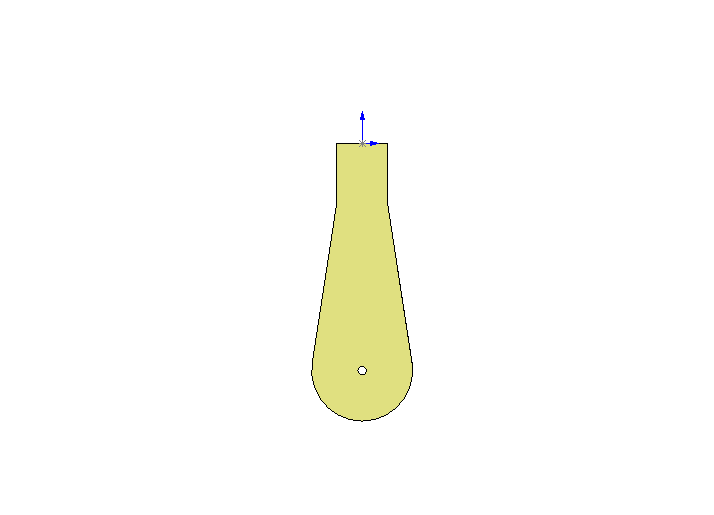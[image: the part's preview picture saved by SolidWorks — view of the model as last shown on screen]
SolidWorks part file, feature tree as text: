
SOLIDWORKS PART (.sldprt)
format: sldprt  version: not decoded by parser v0  size: 144,384 bytes
history: native  units: mm
features: sketch x3, extrude x1, hole x1 (+10 scaffold rows collapsed)
feature tree (15):
  scaffold x10  (default folders/planes/origin — collapsed)
  sketch  "Sketch1"  dims[c1.D2=76.2mm c1.D1=25.4mm c2.D2=355.6mm c2.D1=88.9mm c2.D3=76.2mm c2.D4=25.4mm c2.D5=101.6mm c3.D2=~354.691697mm c3.D4=342.9mm]
  extrude  "Extrude1"  Depth=9.525mm
  hole  "1/2 (0.500000) Diameter Hole2"  Diameter=12.7mm Depth=9.525mm
  sketch  "Sketch5"  dims[D1=19.05mm]
  sketch  "Sketch4"  dims[hole-wizard template sketch: 61 standard entries collapsed; hole parameters above]
decode coverage: 5 of 5 modeling features carry decoded parameters
note: ~ marks probable driven/reference dimensions
note: suppression state not decoded; provenance and decode notes live in map.json
